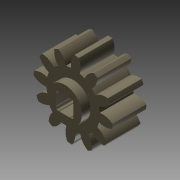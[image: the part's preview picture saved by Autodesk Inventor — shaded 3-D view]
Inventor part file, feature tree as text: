
AUTODESK INVENTOR PART (.ipt)
format: ipt  version: 2013 (Build 170138000, 138)  size: 372,736 bytes
history: native  units: mm (DEFAULTED — no unit token found)
features: sketch x2, imported_body x1, plane x1, other x1, extrude x1
ambient origin geometry x8: Origin, YZ Plane, XZ Plane, XY Plane, X Axis, Y Axis, Z Axis, Center Point
bodies: Solid1 (feature_tree)
feature tree (6):
  imported_body  "Base1"
  plane  "Work Plane1"
  sketch  "Sketch1"  dims[d0=25.4mm d1=0.0mm d2=0.0mm]
  sketch  "Sketch2"  dims[d3=0.0mm]
  other  "Srf1"
  extrude  "ExtrusionSrf1"  TaperAngle=0.0deg  [1 undecoded]
note: 1 required parameter value undecoded (feature->parameter linkage not recoverable at this tier; creation-order binding heuristic only, values carry confidence <= 0.55)
